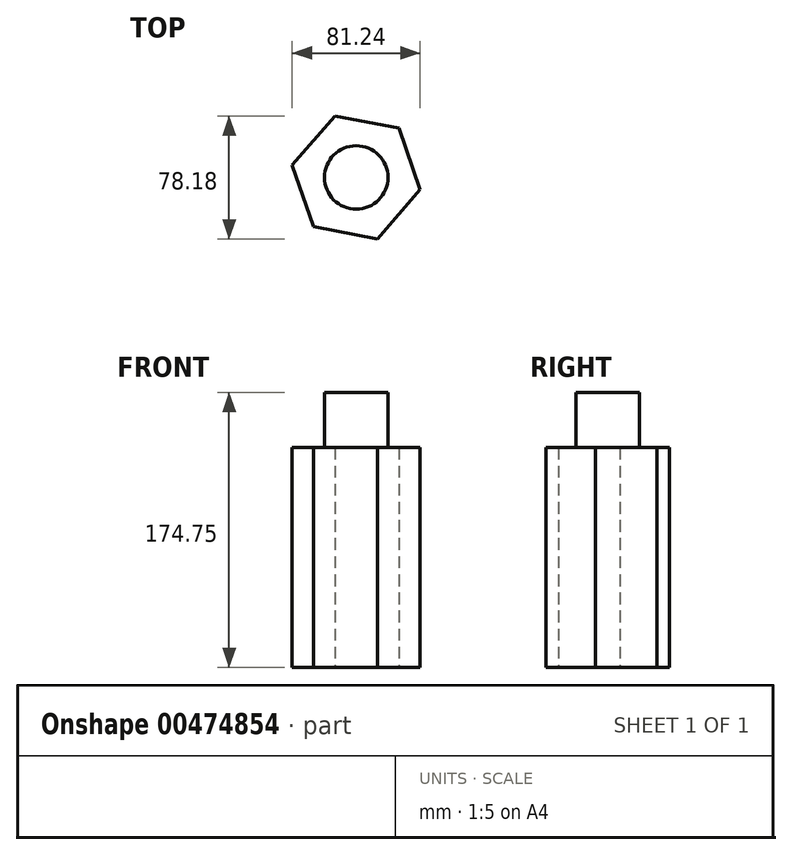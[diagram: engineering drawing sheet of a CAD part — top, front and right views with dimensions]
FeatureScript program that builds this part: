
annotation { "Feature Type Name" : "Feature", "Feature Type Description" : "" }
export const myFeature = defineFeature(function(context is Context, id is Id, definition is map)
    precondition{}
    {
        {
            var Q0;
            Q0=qCreatedBy(makeId("Top.planeOp"),FACE);
            var sketch = newSketch(context, id + "F0", { "sketchPlane" : qUnion([Q0])});
            skCircle(sketch, "E0.cCircle", {"center": v(0, 0) * mm, "radius": 35.82 * mm, "construction": true});
            skLineSegment(sketch, "E0.0", {"start": v(-40.62, 7.83) * mm, "end": v(-13.53, 39.1) * mm});
            skLineSegment(sketch, "E0.1", {"start": v(-13.53, 39.1) * mm, "end": v(27.1, 31.26) * mm});
            skLineSegment(sketch, "E0.2", {"start": v(27.1, 31.26) * mm, "end": v(40.62, -7.83) * mm});
            skLineSegment(sketch, "E0.3", {"start": v(40.62, -7.83) * mm, "end": v(13.53, -39.1) * mm});
            skLineSegment(sketch, "E0.4", {"start": v(13.53, -39.1) * mm, "end": v(-27.1, -31.26) * mm});
            skLineSegment(sketch, "E0.5", {"start": v(-27.1, -31.26) * mm, "end": v(-40.62, 7.83) * mm});
            skPoint(sketch, "E0.0.midPoint", {"position": v(-27.07, 23.46) * mm});
            skCircle(sketch, "E1", {"center": v(0, 0) * mm, "radius": 26.83 * mm});
            skSolve(sketch);
        }
        {
            var Q0;
            Q0=makeQuery(id+"F0.imprint","IMPRINT",FACE,{"disambiguationData":[TD([[makeQuery(id+"F0.imprint","IMPRINT",EDGE,{"derivedFrom":sQuery(id+"F0.wireOp",EDGE,"E1")}),1.0]])]});
            var Q1;
            Q1=makeQuery(id+"F0.imprint","IMPRINT",FACE,{"disambiguationData":[TD([[makeQuery(id+"F0.imprint","IMPRINT",EDGE,{"derivedFrom":sQuery(id+"F0.wireOp",EDGE,"E0.0")}),-1.0]])]});
            extrude(context, id + "F1", {"entities" : qUnion([Q0, Q1]), "depth" : 55.37 * mm});
        }
        {
            var Q0;
            Q0=qCreatedBy(makeId("Top.planeOp"),FACE);
            var sketch = newSketch(context, id + "F2", { "sketchPlane" : qUnion([Q0])});
            skCircle(sketch, "E2", {"center": v(0, 0) * mm, "radius": 20.15 * mm});
            skSolve(sketch);
        }
        {
            var Q0;
            Q0 = qSketchRegion(id + "F2", true);
            extrude(context, id + "F3", {"entities" : qUnion([Q0]), "operationType" : NewBodyOperationType.ADD, "depth" : 90.42 * mm});
        }
        {
            var Q0;
            Q0=makeQuery(id+"F1.opExtrude","CAP_FACE",FACE,{"disambiguationData":[OSD([sQuery(id+"F0.wireOp",EDGE,"E0.0"),sQuery(id+"F0.wireOp",EDGE,"E0.1"),sQuery(id+"F0.wireOp",EDGE,"E0.2"),sQuery(id+"F0.wireOp",EDGE,"E0.3"),sQuery(id+"F0.wireOp",EDGE,"E0.4"),sQuery(id+"F0.wireOp",EDGE,"E0.5")])],"isStart":true});
            extrude(context, id + "F4", {"entities" : qUnion([Q0]), "operationType" : NewBodyOperationType.ADD, "depth" : 84.33 * mm});
        }
    });
